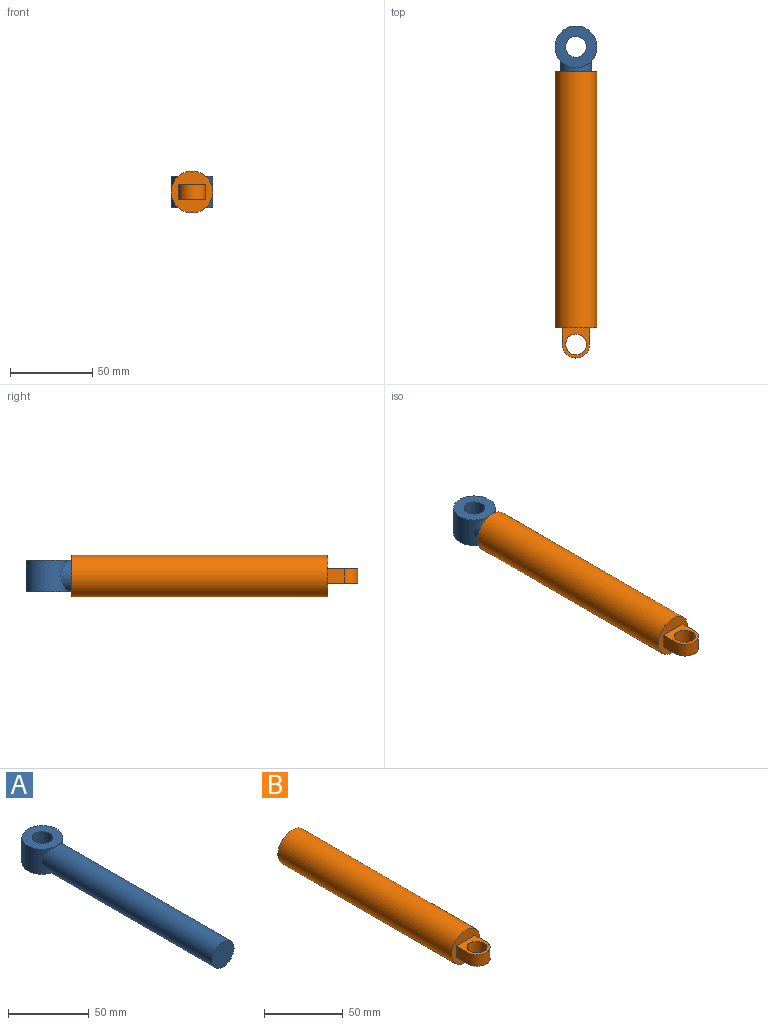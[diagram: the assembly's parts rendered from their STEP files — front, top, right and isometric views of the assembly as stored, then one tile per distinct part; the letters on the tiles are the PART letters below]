
ASSEMBLY  parts=2 mates=1
PART A: 6 faces, bbox 25.4x171.5x19.1 mm
  f0: cylinder r=12.7mm len=25.4mm, axis (0,0,-1), area 1208.8mm2, adj f2,f3,f4
  f1: cylinder r=6.35mm len=19.05mm, axis (0,0,-1), area 760.1mm2, adj f2,f3
  f2: plane 25.4x25.4mm, normal (0,0,1), area 380mm2, adj f0,f1
  f3: plane 25.4x25.4mm, normal (0,0,-1), area 380mm2, adj f0,f1
  f4: cylinder r=9.53mm len=150.35mm, axis (0,1,0), area 8862.8mm2, adj f0,f5
  f5: plane 19.05x19.05mm, normal (0,-1,0), area 285mm2, adj f4
PART B: 11 faces, bbox 25.4x174x25.4 mm
  f0: cylinder r=10.16mm len=152.4mm, axis (0,1,0), area 9728.8mm2, adj f2,f4
  f1: cylinder r=12.7mm len=155.58mm, axis (0,1,0), area 12414.3mm2, adj f2,f3
  f2: plane 25.4x25.4mm, normal (0,1,0), area 182.4mm2, adj f0,f1
  f3: plane 25.4x25.4mm, normal (0,-1,0), area 359.9mm2, adj f1,f5,f6,f9,f10
  f4: plane 20.32x20.32mm, normal (0,1,0), area 324.3mm2, adj f0
  f5: plane 10.16x8.89mm, normal (1,0,0), area 90.3mm2, adj f3,f8,f9,f10
  f6: plane 10.16x8.89mm, normal (-1,0,0), area 90.3mm2, adj f3,f8,f9,f10
  f7: cylinder r=6.35mm len=12.7mm, axis (0,0,-1), area 354.7mm2, adj f9,f10
  f8: cylinder r=8.26mm len=16.51mm, axis (0,0,-1), area 230.6mm2, adj f5,f6,f9,f10
  f9: plane 18.42x16.51mm, normal (0,0,1), area 148.1mm2, adj f3,f5,f6,f7,f8
  f10: plane 18.42x16.51mm, normal (0,0,-1), area 148.1mm2, adj f3,f5,f6,f7,f8
PLACE A rot(axis=(-0.22,-0.13,-0.97),0deg) t=(151.99,175.95,-5.81)mm fixed
PLACE B rot(axis=(-0.22,-0.13,-0.97),0deg) t=(151.99,319.41,-5.81)mm
MATE slider B.f0 <-> A.f4  axis (0,1,0) through (151.99,89.23,-5.81)mm
